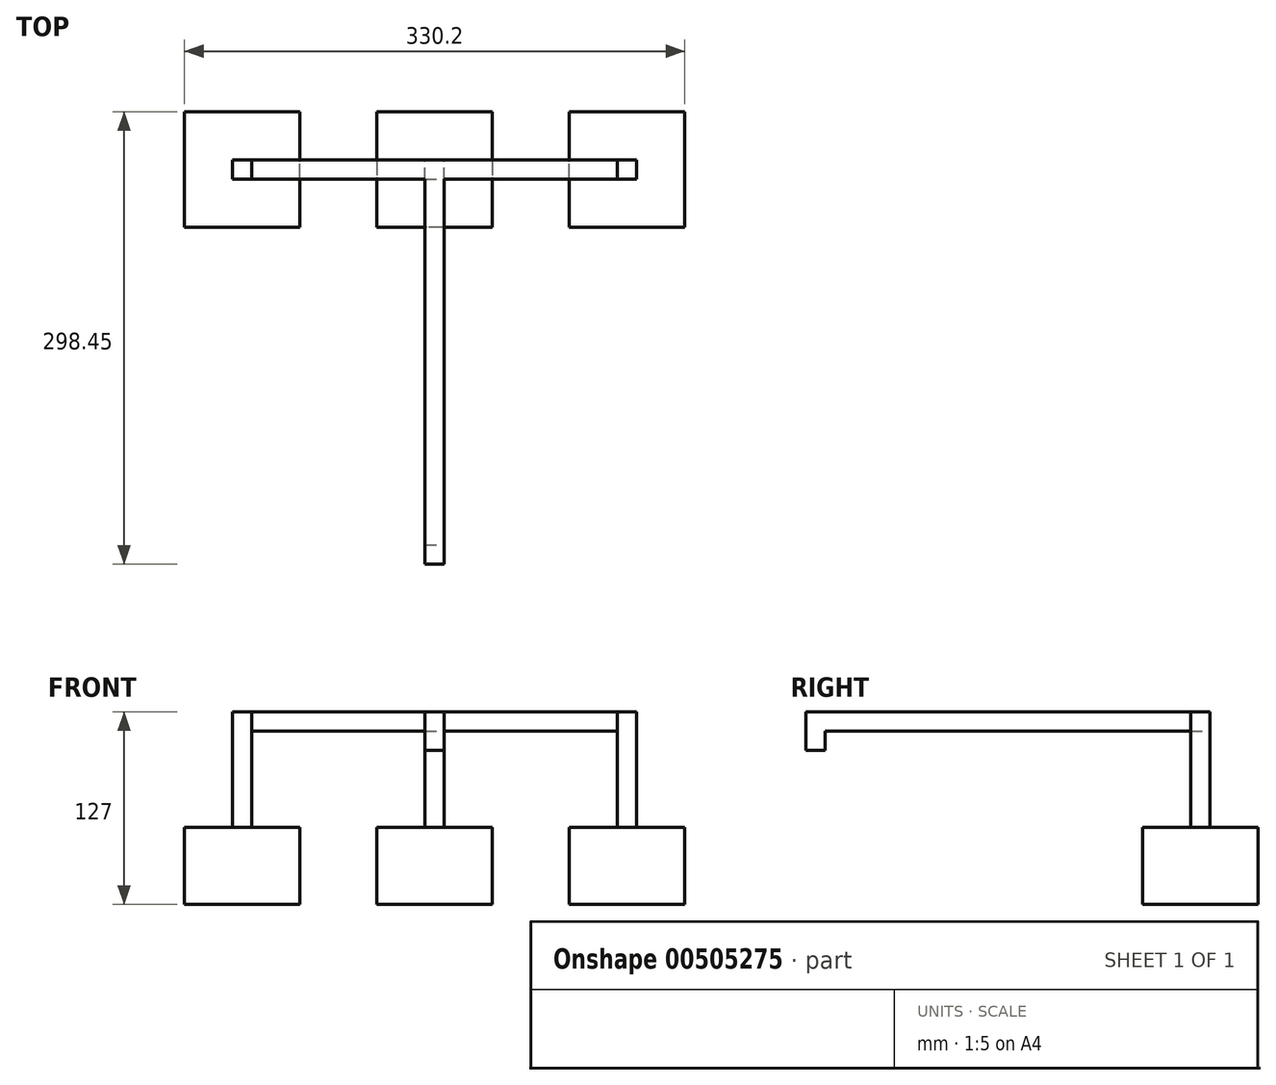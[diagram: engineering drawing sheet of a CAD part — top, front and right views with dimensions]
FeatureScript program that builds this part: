
annotation { "Feature Type Name" : "Feature", "Feature Type Description" : "" }
export const myFeature = defineFeature(function(context is Context, id is Id, definition is map)
    precondition{}
    {
        {
            var Q0;
            Q0=qCreatedBy(makeId("Top.planeOp"),FACE);
            var sketch = newSketch(context, id + "F0", { "sketchPlane" : qUnion([Q0])});
            skLineSegment(sketch, "E0.bottom", {"start": v(38.1, 38.1) * mm, "end": v(-38.1, 38.1) * mm});
            skLineSegment(sketch, "E0.top", {"start": v(38.1, -38.1) * mm, "end": v(-38.1, -38.1) * mm});
            skLineSegment(sketch, "E0.left", {"start": v(38.1, 38.1) * mm, "end": v(38.1, -38.1) * mm});
            skLineSegment(sketch, "E0.right", {"start": v(-38.1, 38.1) * mm, "end": v(-38.1, -38.1) * mm});
            skLineSegment(sketch, "E1.bottom", {"start": v(-88.9, -38.1) * mm, "end": v(-165.1, -38.1) * mm});
            skLineSegment(sketch, "E1.top", {"start": v(-88.9, 38.1) * mm, "end": v(-165.1, 38.1) * mm});
            skLineSegment(sketch, "E1.left", {"start": v(-88.9, -38.1) * mm, "end": v(-88.9, 38.1) * mm});
            skLineSegment(sketch, "E1.right", {"start": v(-165.1, -38.1) * mm, "end": v(-165.1, 38.1) * mm});
            skPoint(sketch, "E2.oppositeSnap0", {"position": v(-127, 38.1) * mm});
            skLineSegment(sketch, "E2.bottom", {"start": v(88.9, -38.1) * mm, "end": v(165.1, -38.1) * mm});
            skLineSegment(sketch, "E2.top", {"start": v(88.9, 38.1) * mm, "end": v(165.1, 38.1) * mm});
            skLineSegment(sketch, "E2.left", {"start": v(88.9, -38.1) * mm, "end": v(88.9, 38.1) * mm});
            skLineSegment(sketch, "E2.right", {"start": v(165.1, -38.1) * mm, "end": v(165.1, 38.1) * mm});
            skSolve(sketch);
        }
        {
            var Q0;
            Q0=makeQuery(id+"F0.imprint","IMPRINT",FACE,{"disambiguationData":[TD([[makeQuery(id+"F0.imprint","IMPRINT",EDGE,{"derivedFrom":sQuery(id+"F0.wireOp",EDGE,"E1.bottom")}),-1.0]])]});
            var Q1;
            Q1=makeQuery(id+"F0.imprint","IMPRINT",FACE,{"disambiguationData":[TD([[makeQuery(id+"F0.imprint","IMPRINT",EDGE,{"derivedFrom":sQuery(id+"F0.wireOp",EDGE,"E0.bottom")}),1.0]])]});
            var Q2;
            Q2=makeQuery(id+"F0.imprint","IMPRINT",FACE,{"disambiguationData":[TD([[makeQuery(id+"F0.imprint","IMPRINT",EDGE,{"derivedFrom":sQuery(id+"F0.wireOp",EDGE,"E2.bottom")}),1.0]])]});
            extrude(context, id + "F1", {"entities" : qUnion([Q0, Q1, Q2]), "depth" : 50.8 * mm});
        }
        {
            var Q0;
            Q0=makeQuery(id+"F1.opExtrude","CAP_FACE",FACE,{"disambiguationData":[OSD([sQuery(id+"F0.wireOp",EDGE,"E0.bottom"),sQuery(id+"F0.wireOp",EDGE,"E0.top"),sQuery(id+"F0.wireOp",EDGE,"E0.left"),sQuery(id+"F0.wireOp",EDGE,"E0.right")])],"isStart":false});
            var sketch = newSketch(context, id + "F2", { "sketchPlane" : qUnion([Q0])});
            skLineSegment(sketch, "E3.bottom", {"start": v(6.35, 6.35) * mm, "end": v(-6.35, 6.35) * mm});
            skLineSegment(sketch, "E3.top", {"start": v(6.35, -6.35) * mm, "end": v(-6.35, -6.35) * mm});
            skLineSegment(sketch, "E3.left", {"start": v(6.35, 6.35) * mm, "end": v(6.35, -6.35) * mm});
            skLineSegment(sketch, "E3.right", {"start": v(-6.35, 6.35) * mm, "end": v(-6.35, -6.35) * mm});
            skPoint(sketch, "E3.middle", {"position": v(0, 0) * mm});
            skSolve(sketch);
        }
        {
            var Q0;
            Q0=makeQuery(id+"F1.opExtrude","CAP_FACE",FACE,{"disambiguationData":[OSD([sQuery(id+"F0.wireOp",EDGE,"E1.bottom"),sQuery(id+"F0.wireOp",EDGE,"E1.top"),sQuery(id+"F0.wireOp",EDGE,"E1.left"),sQuery(id+"F0.wireOp",EDGE,"E1.right")])],"isStart":false});
            var sketch = newSketch(context, id + "F3", { "sketchPlane" : qUnion([Q0])});
            skLineSegment(sketch, "E4.bottom", {"start": v(-120.65, 6.35) * mm, "end": v(-133.35, 6.35) * mm});
            skLineSegment(sketch, "E4.top", {"start": v(-120.65, -6.35) * mm, "end": v(-133.35, -6.35) * mm});
            skLineSegment(sketch, "E4.left", {"start": v(-120.65, 6.35) * mm, "end": v(-120.65, -6.35) * mm});
            skLineSegment(sketch, "E4.right", {"start": v(-133.35, 6.35) * mm, "end": v(-133.35, -6.35) * mm});
            skPoint(sketch, "E4.middle", {"position": v(-127, 0) * mm});
            skPoint(sketch, "E4.middle.positionSnap0", {"position": v(-127, 38.1) * mm});
            skPoint(sketch, "E4.centerSnap0", {"position": v(-127, 38.1) * mm});
            skSolve(sketch);
        }
        {
            var Q0;
            Q0=makeQuery(id+"F1.opExtrude","CAP_FACE",FACE,{"disambiguationData":[OSD([sQuery(id+"F0.wireOp",EDGE,"E2.bottom"),sQuery(id+"F0.wireOp",EDGE,"E2.top"),sQuery(id+"F0.wireOp",EDGE,"E2.left"),sQuery(id+"F0.wireOp",EDGE,"E2.right")])],"isStart":false});
            var sketch = newSketch(context, id + "F4", { "sketchPlane" : qUnion([Q0])});
            skLineSegment(sketch, "E5.bottom", {"start": v(133.35, 6.35) * mm, "end": v(120.65, 6.35) * mm});
            skLineSegment(sketch, "E5.top", {"start": v(133.35, -6.35) * mm, "end": v(120.65, -6.35) * mm});
            skLineSegment(sketch, "E5.left", {"start": v(133.35, 6.35) * mm, "end": v(133.35, -6.35) * mm});
            skLineSegment(sketch, "E5.right", {"start": v(120.65, 6.35) * mm, "end": v(120.65, -6.35) * mm});
            skPoint(sketch, "E5.middle", {"position": v(127, 0) * mm});
            skPoint(sketch, "E5.middle.positionSnap0", {"position": v(127, 38.1) * mm});
            skPoint(sketch, "E5.centerSnap0", {"position": v(127, 38.1) * mm});
            skSolve(sketch);
        }
        {
            var Q0;
            Q0=makeQuery(id+"F3.imprint","IMPRINT",FACE,{"disambiguationData":[TD([[makeQuery(id+"F3.imprint","IMPRINT",EDGE,{"derivedFrom":sQuery(id+"F3.wireOp",EDGE,"E4.bottom")}),1.0]])]});
            var Q1;
            Q1=makeQuery(id+"F2.imprint","IMPRINT",FACE,{"disambiguationData":[TD([[makeQuery(id+"F2.imprint","IMPRINT",EDGE,{"derivedFrom":sQuery(id+"F2.wireOp",EDGE,"E3.bottom")}),1.0]])]});
            var Q2;
            Q2=makeQuery(id+"F4.imprint","IMPRINT",FACE,{"disambiguationData":[TD([[makeQuery(id+"F4.imprint","IMPRINT",EDGE,{"derivedFrom":sQuery(id+"F4.wireOp",EDGE,"E5.bottom")}),1.0]])]});
            extrude(context, id + "F5", {"entities" : qUnion([Q0, Q1, Q2]), "depth" : 76.2 * mm});
        }
        {
            var Q0;
            Q0=makeQuery(id+"F5.opExtrude","SWEPT_FACE",FACE,{"disambiguationData":[OSD([sQuery(id+"F3.wireOp",EDGE,"E4.left")])]});
            var sketch = newSketch(context, id + "F6", { "sketchPlane" : qUnion([Q0])});
            skLineSegment(sketch, "E6.bottom", {"start": v(-6.35, 127) * mm, "end": v(6.35, 127) * mm});
            skLineSegment(sketch, "E6.top", {"start": v(-6.35, 114.3) * mm, "end": v(6.35, 114.3) * mm});
            skLineSegment(sketch, "E6.left", {"start": v(-6.35, 127) * mm, "end": v(-6.35, 114.3) * mm});
            skLineSegment(sketch, "E6.right", {"start": v(6.35, 127) * mm, "end": v(6.35, 114.3) * mm});
            skSolve(sketch);
        }
        {
            var Q0;
            Q0=makeQuery(id+"F5.opExtrude","SWEPT_FACE",FACE,{"disambiguationData":[OSD([sQuery(id+"F2.wireOp",EDGE,"E3.left")])]});
            var sketch = newSketch(context, id + "F7", { "sketchPlane" : qUnion([Q0])});
            skLineSegment(sketch, "E7.bottom", {"start": v(-6.35, 127) * mm, "end": v(6.35, 127) * mm});
            skLineSegment(sketch, "E7.top", {"start": v(-6.35, 114.29) * mm, "end": v(6.35, 114.29) * mm});
            skLineSegment(sketch, "E7.left", {"start": v(-6.35, 127) * mm, "end": v(-6.35, 114.29) * mm});
            skLineSegment(sketch, "E7.right", {"start": v(6.35, 127) * mm, "end": v(6.35, 114.29) * mm});
            skSolve(sketch);
        }
        {
            var Q0;
            Q0=makeQuery(id+"F7.imprint","IMPRINT",FACE,{"disambiguationData":[TD([[makeQuery(id+"F7.imprint","IMPRINT",EDGE,{"derivedFrom":sQuery(id+"F7.wireOp",EDGE,"E7.bottom")}),1.0]])]});
            var Q1;
            Q1=makeQuery(id+"F6.imprint","IMPRINT",FACE,{"disambiguationData":[TD([[makeQuery(id+"F6.imprint","IMPRINT",EDGE,{"derivedFrom":sQuery(id+"F6.wireOp",EDGE,"E6.bottom")}),1.0]])]});
            extrude(context, id + "F8", {"entities" : qUnion([Q0, Q1]), "depth" : 114.3 * mm});
        }
        {
            var Q0;
            Q0=makeQuery(id+"F5.opExtrude","SWEPT_FACE",FACE,{"disambiguationData":[OSD([sQuery(id+"F2.wireOp",EDGE,"E3.top")])]});
            var sketch = newSketch(context, id + "F9", { "sketchPlane" : qUnion([Q0])});
            skLineSegment(sketch, "E8.bottom", {"start": v(-6.35, 127) * mm, "end": v(6.35, 127) * mm});
            skLineSegment(sketch, "E8.top", {"start": v(-6.35, 114.3) * mm, "end": v(6.35, 114.3) * mm});
            skLineSegment(sketch, "E8.left", {"start": v(-6.35, 127) * mm, "end": v(-6.35, 114.3) * mm});
            skLineSegment(sketch, "E8.right", {"start": v(6.35, 127) * mm, "end": v(6.35, 114.3) * mm});
            skSolve(sketch);
        }
        {
            var Q0;
            Q0=makeQuery(id+"F9.imprint","IMPRINT",FACE,{"disambiguationData":[TD([[makeQuery(id+"F9.imprint","IMPRINT",EDGE,{"derivedFrom":sQuery(id+"F9.wireOp",EDGE,"E8.bottom")}),1.0]])]});
            extrude(context, id + "F10", {"entities" : qUnion([Q0]), "operationType" : NewBodyOperationType.ADD, "depth" : 254 * mm});
        }
        {
            var Q0;
            Q0=makeQuery(id+"F10.opExtrude","SWEPT_FACE",FACE,{"disambiguationData":[OSD([sQuery(id+"F9.wireOp",EDGE,"E8.top")])]});
            var sketch = newSketch(context, id + "F11", { "sketchPlane" : qUnion([Q0])});
            skLineSegment(sketch, "E9.bottom", {"start": v(-6.35, 260.35) * mm, "end": v(6.35, 260.35) * mm});
            skLineSegment(sketch, "E9.top", {"start": v(-6.35, 247.65) * mm, "end": v(6.35, 247.65) * mm});
            skLineSegment(sketch, "E9.left", {"start": v(-6.35, 260.35) * mm, "end": v(-6.35, 247.65) * mm});
            skLineSegment(sketch, "E9.right", {"start": v(6.35, 260.35) * mm, "end": v(6.35, 247.65) * mm});
            skSolve(sketch);
        }
        {
            var Q0;
            Q0=makeQuery(id+"F11.imprint","IMPRINT",FACE,{"disambiguationData":[TD([[makeQuery(id+"F11.imprint","IMPRINT",EDGE,{"derivedFrom":sQuery(id+"F11.wireOp",EDGE,"E9.bottom")}),-1.0]])]});
            extrude(context, id + "F12", {"entities" : qUnion([Q0]), "operationType" : NewBodyOperationType.ADD, "depth" : 12.7 * mm});
        }
    });
